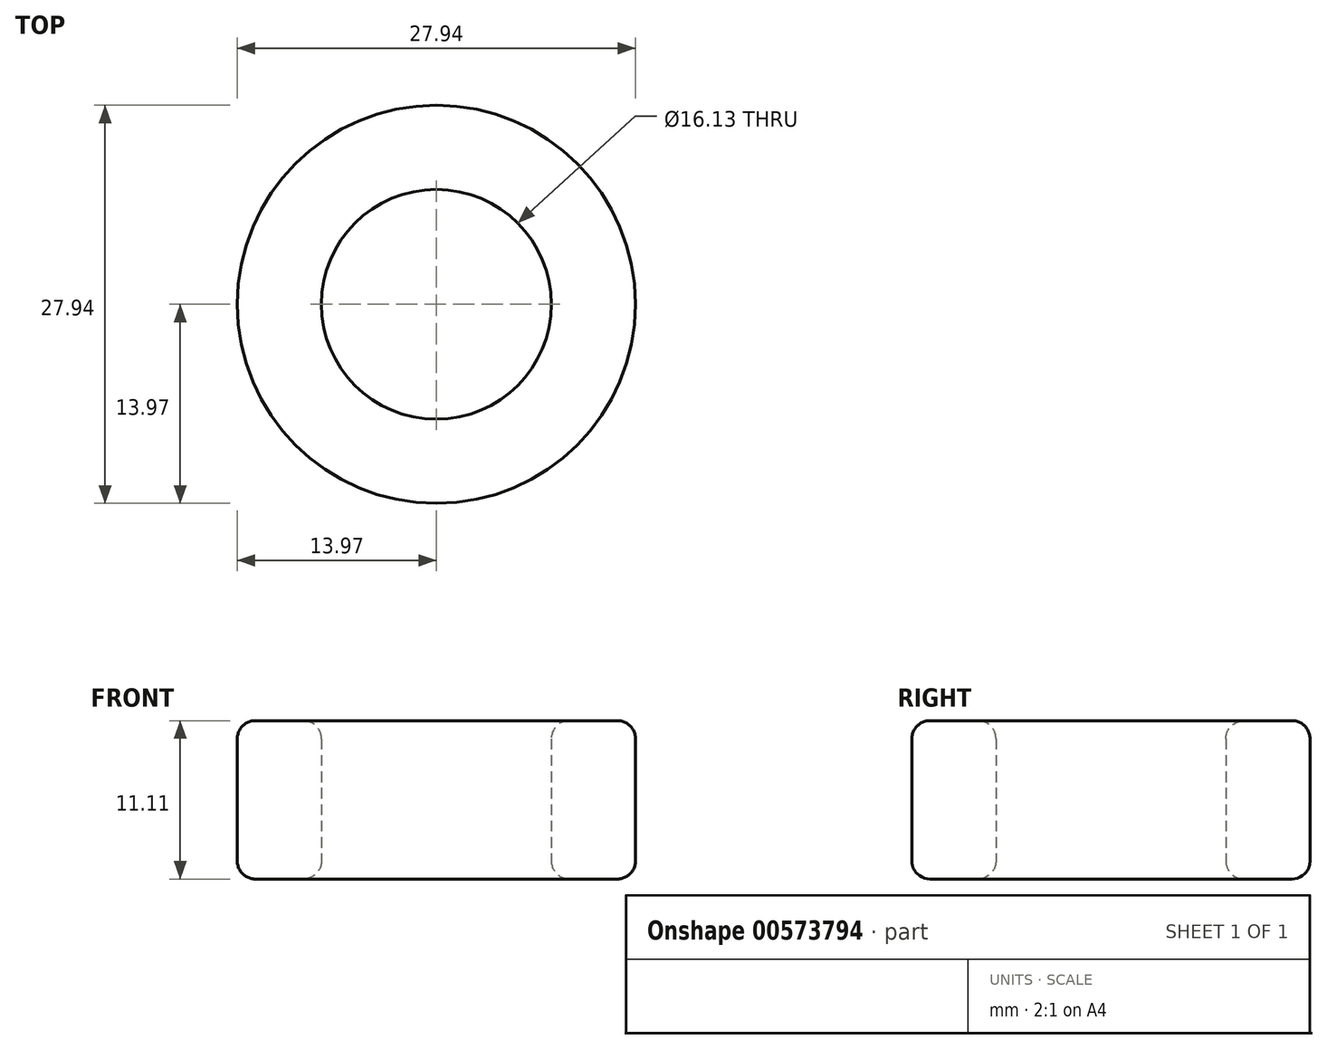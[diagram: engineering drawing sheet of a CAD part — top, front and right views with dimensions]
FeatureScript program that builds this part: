
annotation { "Feature Type Name" : "Feature", "Feature Type Description" : "" }
export const myFeature = defineFeature(function(context is Context, id is Id, definition is map)
    precondition{}
    {
        {
            var Q0;
            Q0=qCreatedBy(makeId("Top.planeOp"),FACE);
            var sketch = newSketch(context, id + "F0", { "sketchPlane" : qUnion([Q0])});
            skCircle(sketch, "E0", {"center": v(0, 0) * mm, "radius": 8.06 * mm});
            skCircle(sketch, "E1", {"center": v(0, 0) * mm, "radius": 13.97 * mm});
            skSolve(sketch);
        }
        {
            var Q0;
            Q0=qSketchRegion(id+"F0",true);
            extrude(context, id + "F1", {"entities" : qUnion([Q0]), "depth" : 11.1 * mm, "offsetDistance" : 25.4 * mm});
        }
        {
            var Q0;
            Q0=makeQuery(id+"F1.opExtrude","SWEPT_FACE",FACE,{"disambiguationData":[OSD([sQuery(id+"F0.wireOp",EDGE,"E1")])]});
            var Q1;
            Q1=makeQuery(id+"F1.opExtrude","CAP_EDGE",EDGE,{"disambiguationData":[OSD([sQuery(id+"F0.wireOp",EDGE,"E0")])],"isStart":false});
            var Q2;
            Q2=makeQuery(id+"F1.opExtrude","CAP_EDGE",EDGE,{"disambiguationData":[OSD([sQuery(id+"F0.wireOp",EDGE,"E0")])],"isStart":true});
            fillet(context, id + "F2", {"entities" : qUnion([Q0, Q1, Q2]), "radius" : 1.27 * mm, "tangentPropagation" : true, "allowEdgeOverflow" : false});
        }
    });
